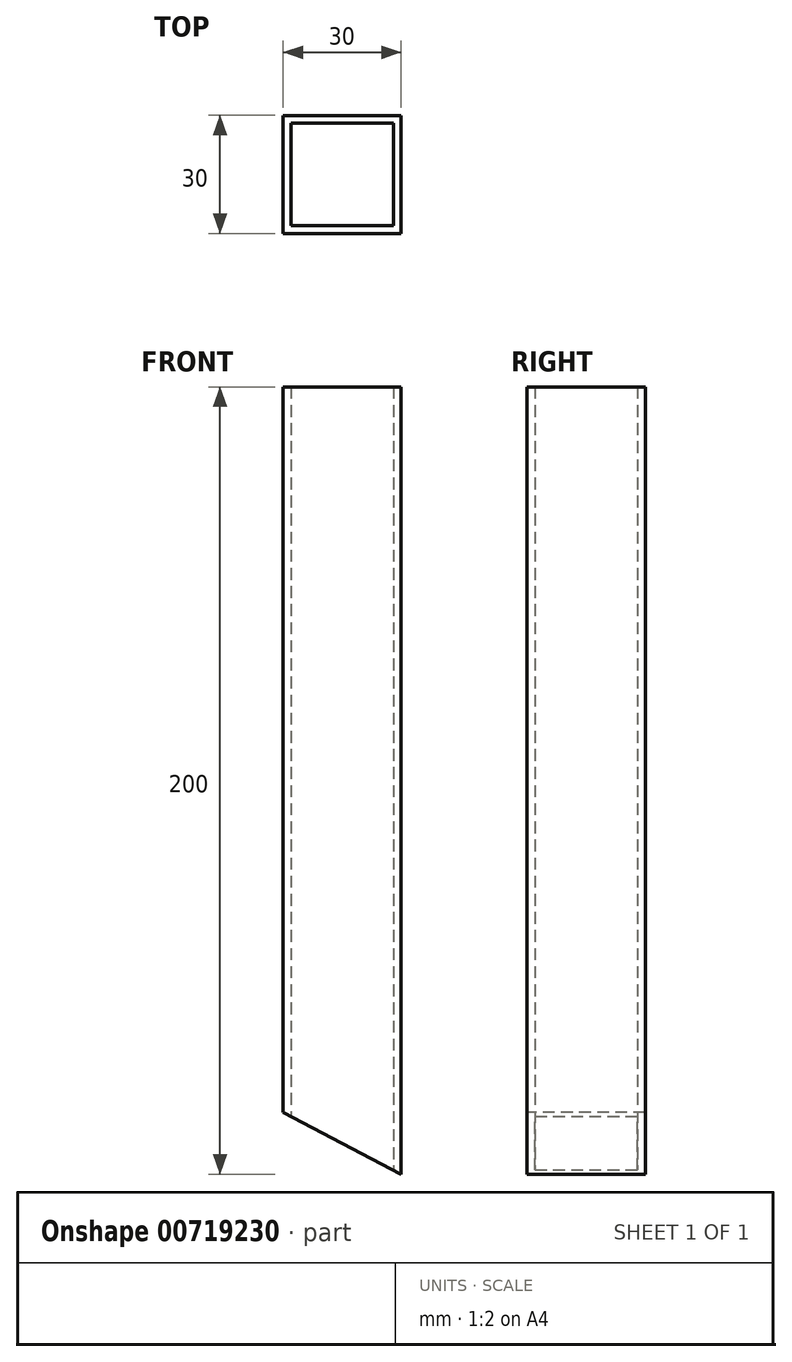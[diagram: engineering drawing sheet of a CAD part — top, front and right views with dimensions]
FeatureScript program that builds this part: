
annotation { "Feature Type Name" : "Feature", "Feature Type Description" : "" }
export const myFeature = defineFeature(function(context is Context, id is Id, definition is map)
    precondition{}
    {
        {
            var Q0;
            Q0=qCreatedBy(makeId("Top.planeOp"),FACE);
            var sketch = newSketch(context, id + "F0", { "sketchPlane" : qUnion([Q0])});
            skLineSegment(sketch, "E0.bottom", {"start": v(0, 1.6) * mm, "end": v(-30, 1.6) * mm});
            skLineSegment(sketch, "E0.top", {"start": v(0, 31.6) * mm, "end": v(-30, 31.6) * mm});
            skLineSegment(sketch, "E0.left", {"start": v(0, 1.6) * mm, "end": v(0, 31.6) * mm});
            skLineSegment(sketch, "E0.right", {"start": v(-30, 1.6) * mm, "end": v(-30, 31.6) * mm});
            skLineSegment(sketch, "E1.0", {"start": v(-28, 3.6) * mm, "end": v(-28, 29.6) * mm});
            skLineSegment(sketch, "E1.1", {"start": v(-2, 3.6) * mm, "end": v(-28, 3.6) * mm});
            skLineSegment(sketch, "E1.2", {"start": v(-2, 3.6) * mm, "end": v(-2, 29.6) * mm});
            skLineSegment(sketch, "E1.3", {"start": v(-2, 29.6) * mm, "end": v(-28, 29.6) * mm});
            skSolve(sketch);
        }
        {
            var Q0;
            Q0=makeQuery(id+"F0.imprint","IMPRINT",FACE,{"disambiguationData":[TD([[makeQuery(id+"F0.imprint","IMPRINT",EDGE,{"derivedFrom":sQuery(id+"F0.wireOp",EDGE,"E0.bottom")}),-1.0]])]});
            extrude(context, id + "F1", {"entities" : qUnion([Q0]), "depth" : 200 * mm, "offsetDistance" : 25 * mm});
        }
        {
            var Q0;
            Q0=makeQuery(id+"F1.opExtrude","SWEPT_FACE",FACE,{"disambiguationData":[OSD([sQuery(id+"F0.wireOp",EDGE,"E0.bottom")])]});
            var sketch = newSketch(context, id + "F2", { "sketchPlane" : qUnion([Q0])});
            skLineSegment(sketch, "E2", {"start": v(0, 0) * mm, "end": v(-30, 15.75) * mm});
            skSolve(sketch);
        }
        {
            var Q0;
            {var subQ0=sQuery(id+"F2.wireOp",EDGE,"E2");Q0=makeQuery(id+"F2.imprint","IMPRINT",FACE,{"disambiguationData":[TD([[makeQuery(id+"F2.imprint","IMPRINT",EDGE,{"derivedFrom":subQ0}),1.0]])]});}
            var Q1;
            Q1=makeQuery(id+"F1.opExtrude","SWEPT_FACE",FACE,{"disambiguationData":[OSD([sQuery(id+"F0.wireOp",EDGE,"E0.top")])]});
            extrude(context, id + "F3", {"entities" : qUnion([Q0]), "operationType" : NewBodyOperationType.REMOVE, "endBound" : BoundingType.UP_TO_SURFACE, "oppositeDirection" : true, "depth" : 25 * mm, "endBoundEntityFace" : qUnion([Q1]), "offsetDistance" : 25 * mm});
        }
    });
